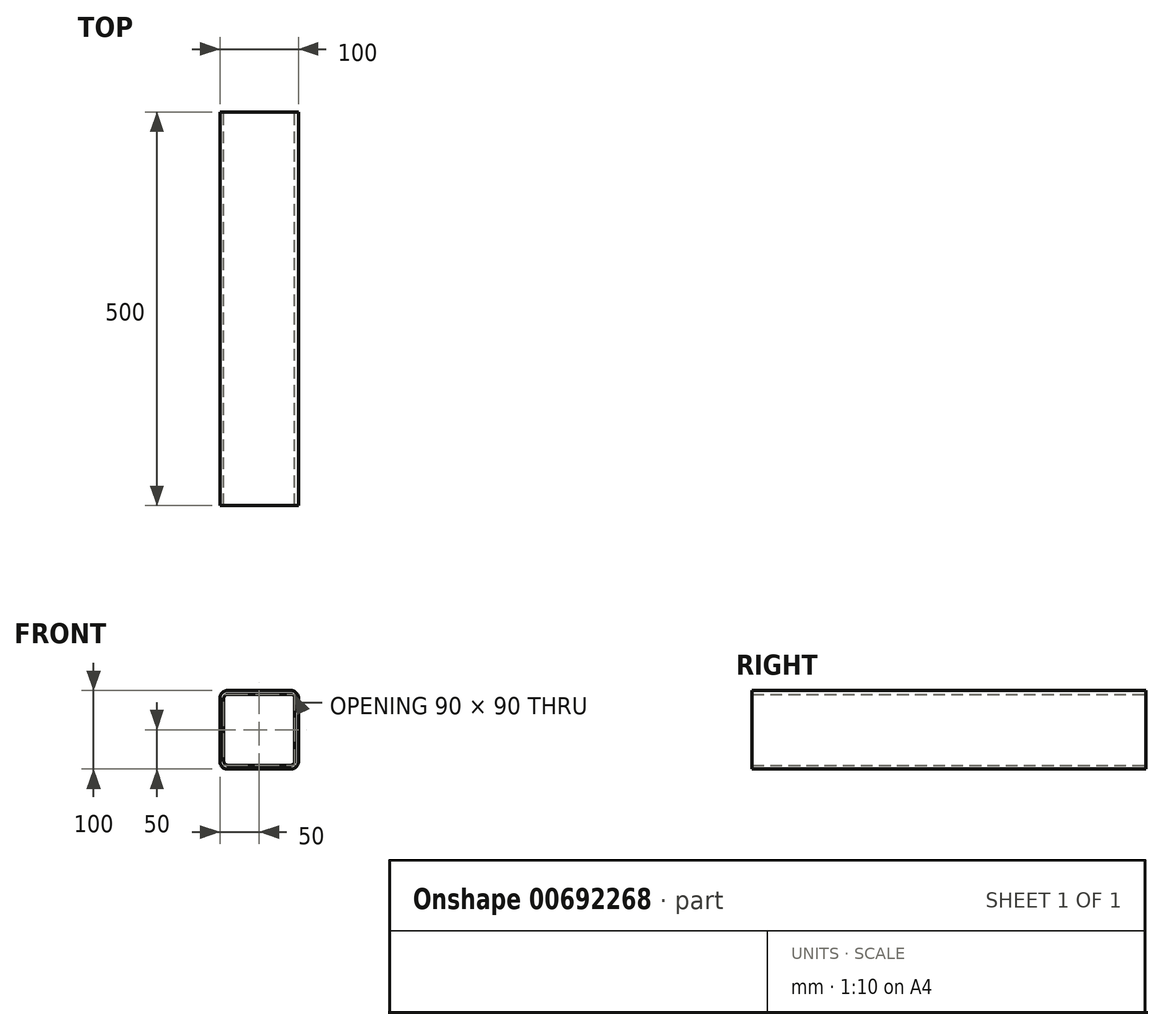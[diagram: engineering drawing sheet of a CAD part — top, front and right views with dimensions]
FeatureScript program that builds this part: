
annotation { "Feature Type Name" : "Feature", "Feature Type Description" : "" }
export const myFeature = defineFeature(function(context is Context, id is Id, definition is map)
    precondition{}
    {
        {
            var Q0;
            Q0=qCreatedBy(makeId("Front.planeOp"),FACE);
            var sketch = newSketch(context, id + "F0", { "sketchPlane" : qUnion([Q0])});
            skLineSegment(sketch, "E0.bottom", {"start": v(10, 0) * mm, "end": v(90, 0) * mm});
            skLineSegment(sketch, "E0.top", {"start": v(10, 100) * mm, "end": v(90, 100) * mm});
            skLineSegment(sketch, "E0.left", {"start": v(0, 10) * mm, "end": v(0, 90) * mm});
            skLineSegment(sketch, "E0.right", {"start": v(100, 10) * mm, "end": v(100, 90) * mm});
            skPoint(sketch, "E1.visualSharp", {"position": v(0, 100) * mm});
            skArc(sketch, "E1.filletArc", {"start": v(10, 100) * mm, "mid": v(2.93, 97.07) * mm, "end": v(0, 90) * mm});
            skPoint(sketch, "E2.visualSharp", {"position": v(100, 100) * mm});
            skArc(sketch, "E2.filletArc", {"start": v(100, 90) * mm, "mid": v(97.07, 97.07) * mm, "end": v(90, 100) * mm});
            skPoint(sketch, "E3.visualSharp", {"position": v(100, 0) * mm});
            skArc(sketch, "E3.filletArc", {"start": v(90, 0) * mm, "mid": v(97.07, 2.93) * mm, "end": v(100, 10) * mm});
            skPoint(sketch, "E4.visualSharp", {"position": v(0, 0) * mm});
            skArc(sketch, "E4.filletArc", {"start": v(0, 10) * mm, "mid": v(2.93, 2.93) * mm, "end": v(10, 0) * mm});
            skArc(sketch, "E5.0", {"start": v(10, 95) * mm, "mid": v(6.46, 93.54) * mm, "end": v(5, 90) * mm});
            skLineSegment(sketch, "E5.1", {"start": v(5, 10) * mm, "end": v(5, 90) * mm});
            skLineSegment(sketch, "E5.2", {"start": v(10, 95) * mm, "end": v(90, 95) * mm});
            skArc(sketch, "E5.3", {"start": v(5, 10) * mm, "mid": v(6.46, 6.46) * mm, "end": v(10, 5) * mm});
            skArc(sketch, "E5.4", {"start": v(95, 90) * mm, "mid": v(93.54, 93.54) * mm, "end": v(90, 95) * mm});
            skLineSegment(sketch, "E5.5", {"start": v(95, 10) * mm, "end": v(95, 90) * mm});
            skArc(sketch, "E5.6", {"start": v(90, 5) * mm, "mid": v(93.54, 6.46) * mm, "end": v(95, 10) * mm});
            skLineSegment(sketch, "E5.7", {"start": v(10, 5) * mm, "end": v(90, 5) * mm});
            skSolve(sketch);
        }
        {
            var Q0;
            Q0 = qSketchRegion(id + "F0", true);
            extrude(context, id + "F1", {"entities" : qUnion([Q0]), "depth" : 500 * mm, "offsetDistance" : 25 * mm});
        }
    });
